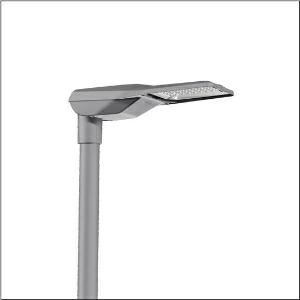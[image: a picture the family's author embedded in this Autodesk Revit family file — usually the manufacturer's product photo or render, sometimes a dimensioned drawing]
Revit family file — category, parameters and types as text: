
# Revit family: streetlight_sl_21_iq_mini___p1_0a_5xe2a41g08hb_15d1
name_source: partatom
category: Lighting Fixtures
units: mm (PartAtom-declared; Revit-internal decimal feet)

## family parameters
Cut with Voids When Loaded = No
Host = Face
Light Source = No
Part Type = Normal
Room Calculation Point = No
Round Connector Dimension = Use Diameter
Shared = No

## types (1)
- --- (1 x LED, 9860 lm, 70.9 W, 4000K)
    Apparent Load = 71 VA
    CIE Flux Codes = 21 50 90 100 100
    Color Rendering = 70
    Color Temperature = 4000K
    Default Elevation = 1800 mm
    Description = Streetlight SL 21 iQ mini, mast luminaire, primary light control with lens, of PMMA, primary optical cover: cover, of toughened safety glass, transparent, light distribution: P1.0a, light emission: direct distribution, primary light characteristic: asymmetric, installation type: post-top, side-entry, LED, High Power LED, rated luminous flux: 9.860lm, luminous efficacy: 139lm/W, light colour: 740, colour temperature: 4000K, control: Street-Remote, Auto-Match, Temp-Guard, Lumen-Switch, Night-Set, Smart-Wire, Light-Fading, Desk-Remote (wireless, voltage-free reading and setting of iQ features in the workshop via application-optimized NFC function/RFID function), optimised constant luminous flux control (CLO 2.0), presetting dimming linear, mains connection: 220..240V, AC, 50/60Hz, start of lifetime: 71W, end of service life: 75W, reduction: 31W, luminaire housing, of diecast aluminium, powder-coated, Siteco® metallic grey (DB 702S), corrosivity category C5 mid according to DIN EN ISO 12944, please order mast flange separately, inclination adjustable: 0°, 5°, 10°, 15°, sealing non-destructively replaceable, multi-level sealing system, length: 628mm, width: 235mm, height: 110mm, mast flange for spigot size: 42mm (side-entry): 5XC10008XM4, 60/48mm (side-entry/post-top): 5XC10108XM2, 76/60mm (side-entry/post-top): 5XC10108XM1, protection rating (complete): IP66, insulation class (complete): insulation class II (safety insulation), certification: CE, ENEC, ENEC+, VDE, impact resistance: IK09, permissible operating ambient temperature for outdoor applications: -40..+50°C, standard-compliant lighting for roads and squares, packaging unit: 1 piece

Light Distribution: P1.0a
    Height = 110 mm
    Lamp = 1 x LED
    Lamp Light Flux = 9860 lm
    Lamp Power = 70.9 W
    Lamp count = 1
    Length = 625 mm
    Luminous efficacy = 139 lm/W
    Manufacturer = Siteco
    ModVariant = No
    Model = 5XE2A41G08HB
    Number of Poles = 1
    OnlyDefault = Yes
    Power Factor = 1
    Product Name = Streetlight SL 21 iQ mini | P1.0a
    Product group = mast luminaire | pylon top
    ProductGroupID = 6100
    Protection Class = Protection class II
    Protection Degree = IP 66
    RLX_Detail_Level = 1
    RLX_Emergency_Light_Flux = 0 lm
    RLX_Emergency_Type = 0
    RLX_Emergency_Type_DB = No
    RlxData = <blob elided: 103465 chars, md5=c828f417>
    Socket = socket
    Standby Power = 0 W
    System Light Flux = 9860 lm
    System Power = 71 W
    Type Comments = factory setting: luminous flux: 100 % | dim-lin: 254 | 711 mA
    Type Image = l_1003519.jpg
    URL = http://relux.com
    VarID = @adj_089925
    Voltage = 0 V
    Weight = 0.00 kg
    Width = 234 mm

## geometry (parser evidence)
native form markers: Blend x4, Sweep x11
no freeform markers — native parametric forms only
